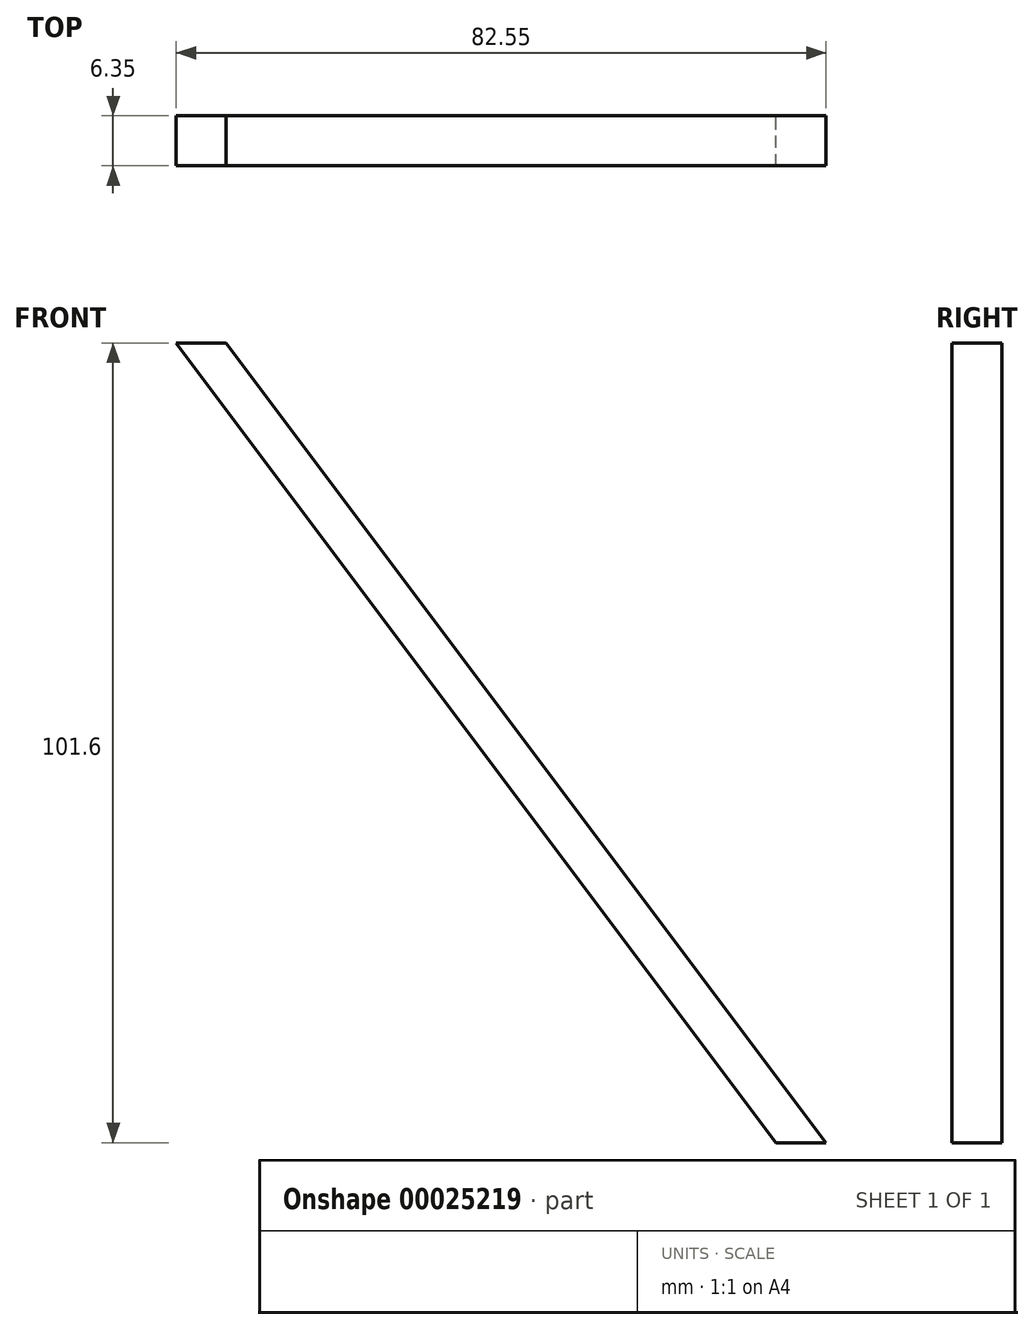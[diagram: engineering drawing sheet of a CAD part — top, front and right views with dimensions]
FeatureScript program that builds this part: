
annotation { "Feature Type Name" : "Feature", "Feature Type Description" : "" }
export const myFeature = defineFeature(function(context is Context, id is Id, definition is map)
    precondition{}
    {
        {
            var Q0;
            Q0=qCreatedBy(makeId("Front.planeOp"),FACE);
            var sketch = newSketch(context, id + "F0", { "sketchPlane" : qUnion([Q0])});
            skLineSegment(sketch, "E0", {"start": v(-76.2, 101.6) * mm, "end": v(0, 0) * mm});
            skLineSegment(sketch, "E1", {"start": v(-76.2, 101.6) * mm, "end": v(-82.55, 101.6) * mm});
            skLineSegment(sketch, "E2", {"start": v(0, 0) * mm, "end": v(-6.35, 0) * mm});
            skLineSegment(sketch, "E3", {"start": v(-6.35, 0) * mm, "end": v(-82.55, 101.6) * mm});
            skSolve(sketch);
        }
        {
            var Q0;
            Q0=makeQuery(id+"F0.imprint","IMPRINT",FACE,{"disambiguationData":[TD([[makeQuery(id+"F0.imprint","IMPRINT",EDGE,{"derivedFrom":sQuery(id+"F0.wireOp",EDGE,"E0")}),-1.0]])]});
            extrude(context, id + "F1", {"entities" : qUnion([Q0]), "depth" : 6.35 * mm});
        }
    });
